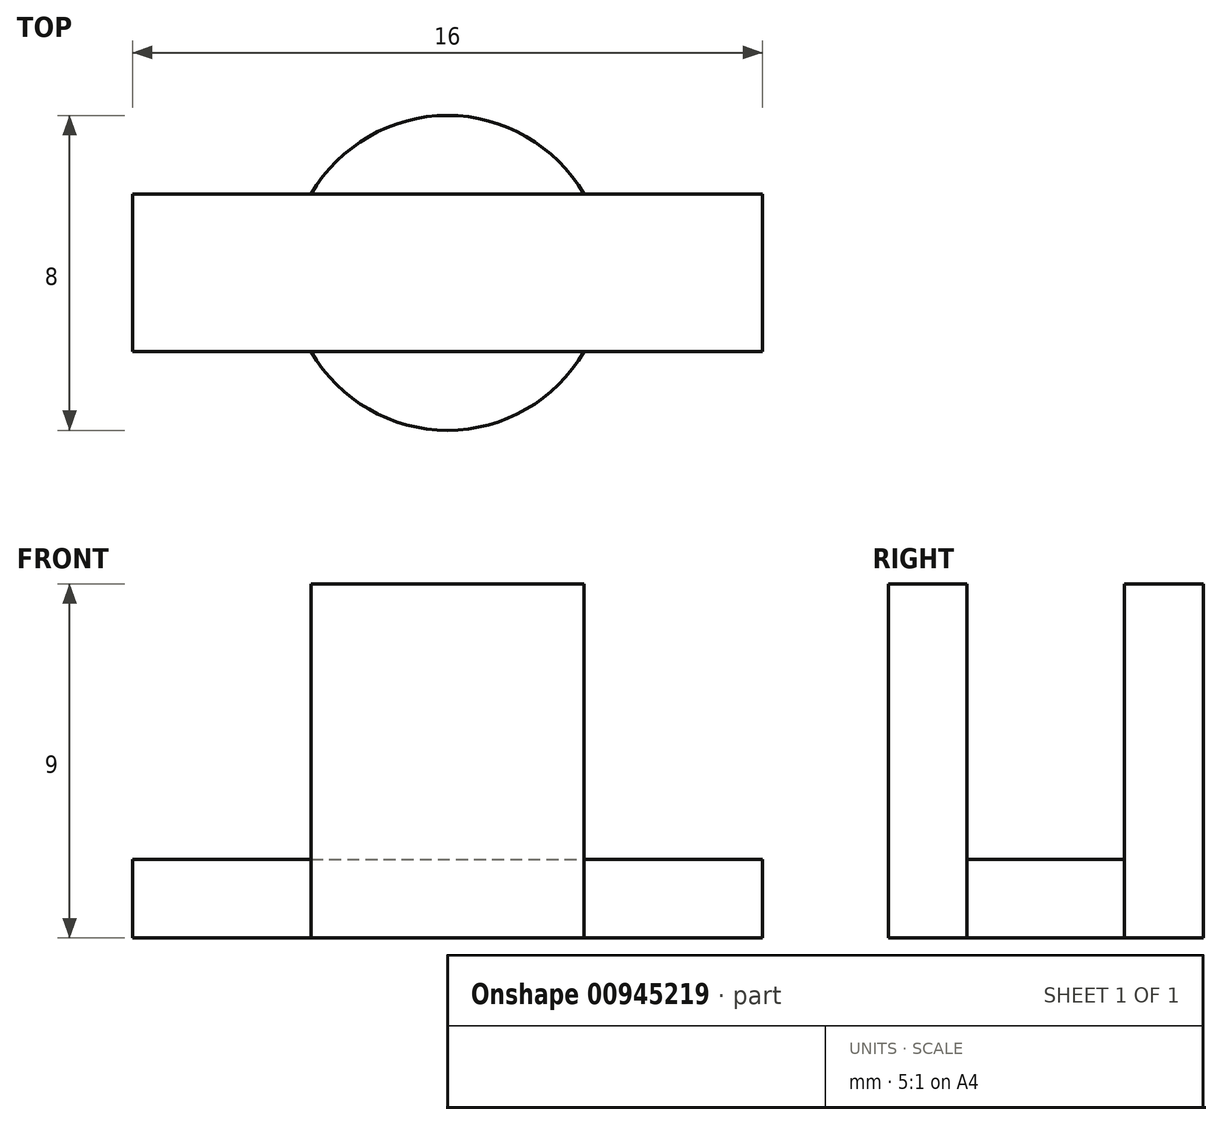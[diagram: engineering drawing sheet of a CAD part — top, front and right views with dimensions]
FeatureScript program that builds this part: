
annotation { "Feature Type Name" : "Feature", "Feature Type Description" : "" }
export const myFeature = defineFeature(function(context is Context, id is Id, definition is map)
    precondition{}
    {
        {
            var Q0;
            Q0=qCreatedBy(makeId("Top.planeOp"),FACE);
            var sketch = newSketch(context, id + "F0", { "sketchPlane" : qUnion([Q0])});
            skCircle(sketch, "E0", {"center": v(0, 0) * mm, "radius": 4 * mm});
            skLineSegment(sketch, "E1.bottom", {"start": v(-8, -2) * mm, "end": v(8, -2) * mm});
            skLineSegment(sketch, "E1.top", {"start": v(-8, 2) * mm, "end": v(8, 2) * mm});
            skLineSegment(sketch, "E1.left", {"start": v(-8, -2) * mm, "end": v(-8, 2) * mm});
            skLineSegment(sketch, "E1.right", {"start": v(8, -2) * mm, "end": v(8, 2) * mm});
            skSolve(sketch);
        }
        {
            var Q0;
            {var subQ0=sQuery(id+"F0.wireOp",EDGE,"E1.top");var subQ1=sQuery(id+"F0.wireOp",EDGE,"E0");var subQ2=makeQuery(id+"F0.imprint","INTERSECT",VERTEX,{"disambiguationData":[OD(0.0)],"derivedFrom":[subQ1,subQ0]});Q0=makeQuery(id+"F0.imprint","IMPRINT",FACE,{"disambiguationData":[TD([[makeQuery(id+"F0.imprint","IMPRINT",EDGE,{"disambiguationData":[TD([[subQ2,1.0]])],"derivedFrom":subQ1}),1.0]])]});}
            var Q1;
            {var subQ0=sQuery(id+"F0.wireOp",EDGE,"E1.bottom");var subQ1=sQuery(id+"F0.wireOp",EDGE,"E0");var subQ2=makeQuery(id+"F0.imprint","INTERSECT",VERTEX,{"disambiguationData":[OD(0.0)],"derivedFrom":[subQ1,subQ0]});Q1=makeQuery(id+"F0.imprint","IMPRINT",FACE,{"disambiguationData":[TD([[makeQuery(id+"F0.imprint","IMPRINT",EDGE,{"disambiguationData":[TD([[subQ2,-1.0]])],"derivedFrom":subQ1}),1.0]])]});}
            var Q2;
            {var subQ0=sQuery(id+"F0.wireOp",EDGE,"E0");var subQ1=makeQuery(id+"F0.imprint","IMPRINT",VERTEX,{"derivedFrom":subQ0});Q2=makeQuery(id+"F0.imprint","IMPRINT",FACE,{"disambiguationData":[TD([[makeQuery(id+"F0.imprint","IMPRINT",EDGE,{"disambiguationData":[TD([[subQ1,-1.0]])],"derivedFrom":subQ0}),1.0]])]});}
            extrude(context, id + "F1", {"entities" : qUnion([Q0, Q1, Q2]), "depth" : 9 * mm, "offsetDistance" : 25 * mm});
        }
        {
            var Q0;
            Q0 = qSketchRegion(id + "F0", true);
            extrude(context, id + "F2", {"entities" : qUnion([Q0]), "operationType" : NewBodyOperationType.ADD, "depth" : 2 * mm, "offsetDistance" : 25 * mm});
        }
    });
